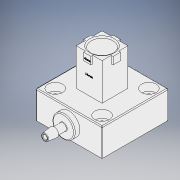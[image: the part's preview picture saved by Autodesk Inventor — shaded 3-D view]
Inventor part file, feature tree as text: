
AUTODESK INVENTOR PART (.ipt)
format: ipt  version: 2019 (Build 230136000, 136)  size: 586,752 bytes
history: native  units: mm
features: sketch x11, extrude x6, projected_geometry x4, plane x3, revolve x2, fillet x2, sweep x1, hole x1, pattern_circular x1
ambient origin geometry x8: Origin, YZ Plane, XZ Plane, XY Plane, X Axis, Y Axis, Z Axis, Center Point
bodies: Solid1 (feature_tree)
feature tree (31):
  revolve  "Revolution1"  [1 undecoded]
  plane  "Work Plane1"
  extrude  "Extrusion1"  Depth=0.35mm
  plane  "Work Plane7"
  extrude  "Extrusion6"  Depth=0.75mm
  extrude  "Extrusion7"  TaperAngle=90.0deg  [1 undecoded]
  sketch  "Sketch17"  dims[d11=0.0mm d14=2.0mm d15=0.0mm d45=0.0mm]
  plane  "Work Plane8"
  sweep  "Sweep3"
  fillet  "Fillet1"  [1 undecoded]
  hole  "Hole3"  [1 undecoded]
  revolve  "Revolution2"  [1 undecoded]
  fillet  "Fillet2"  Radius=32.7mm
  extrude  "Extrusion13"  Depth=3.0mm
  pattern_circular  "Circular Pattern1"  [2 undecoded]
  extrude  "Extrusion14"  Depth=6.0mm
  extrude  "Extrusion15"  Depth=5.0mm
  sketch  "Sketch1"  dims[d0=7.0mm d1=20.0mm]
  sketch  "Sketch2"  dims[d5=12.0mm d6=0.35mm]
  sketch  "Sketch11"  dims[d7=0.75mm d8=0.75mm]
  sketch  "Sketch16"  dims[d9=0.75mm d10=90.0deg]
  projected_geometry  "Projected Loop9"
  sketch  "Sketch18"  dims[d47=15.0mm d48=0.0mm d60=36.0mm]
  sketch  "Sketch19"  dims[d61=36.0mm d64=8.45mm d65=32.7mm d66=0.0mm]
  sketch  "Sketch21"  dims[d67=0.0mm d68=0.0mm d69=3.0mm]
  sketch  "Sketch28"  dims[d70=25.4mm]
  projected_geometry  "Projected Loop13"
  sketch  "Sketch30"  dims[d71=25.4mm]
  projected_geometry  "Projected Loop15"
  sketch  "Sketch31"  dims[d72=4.496mm d73=6.0mm d74=7.938mm d75=4.166mm d76=90.0deg d77=19.05mm d78=20.594885mm d79=3.0mm d80=6.0mm d81=5.0mm d82=1.8796mm d83=0.25mm d84=2.413mm d85=5.08mm d86=1.15mm d87=0.25mm d88=0.25mm d89=90.0deg d90=0.5mm d124=0.0mm d125=0.0mm d126=4.0mm d127=1.0mm d128=0.0mm d129=40.0mm d130=360.0deg d132=1.010217mm d133=0.5mm d134=0.0mm d135=0.5mm d136=0.0mm]
  projected_geometry  "Projected Loop16"
note: 7 required parameter values undecoded (feature->parameter linkage not recoverable at this tier; creation-order binding heuristic only, values carry confidence <= 0.55)